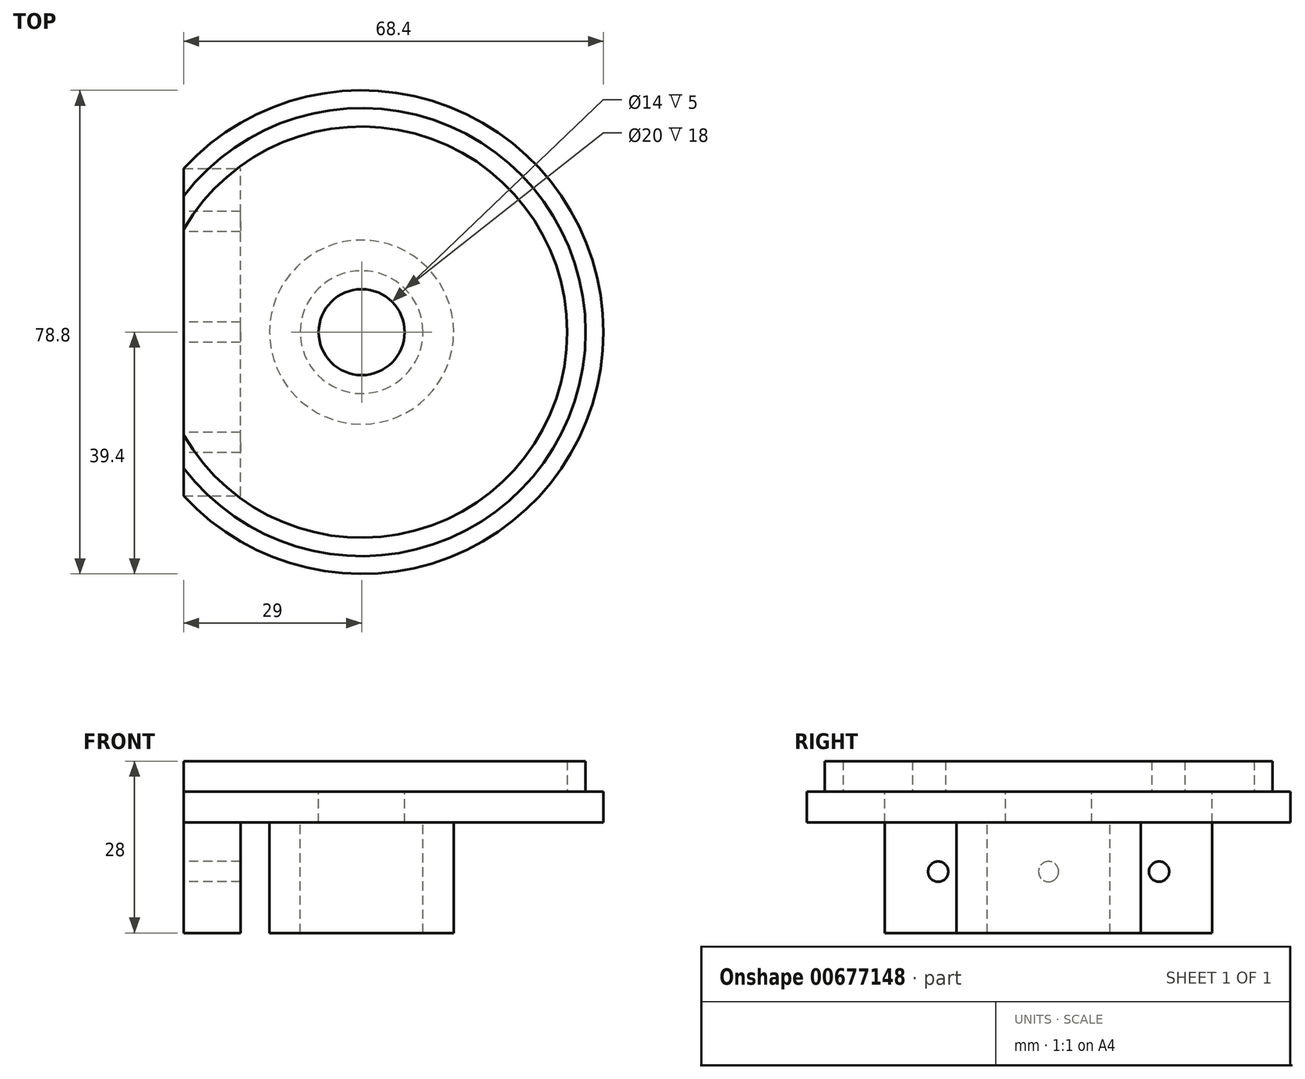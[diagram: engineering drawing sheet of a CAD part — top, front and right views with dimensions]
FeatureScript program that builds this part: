
annotation { "Feature Type Name" : "Feature", "Feature Type Description" : "" }
export const myFeature = defineFeature(function(context is Context, id is Id, definition is map)
    precondition{}
    {
        {
            var Q0;
            Q0=qCreatedBy(makeId("Top.planeOp"),FACE);
            var sketch = newSketch(context, id + "F0", { "sketchPlane" : qUnion([Q0])});
            skArc(sketch, "E0", {"start": v(-29, -26.67) * mm, "mid": v(39.4, 0) * mm, "end": v(-29, 26.67) * mm});
            skArc(sketch, "E1", {"start": v(-29, -22.16) * mm, "mid": v(36.5, 0) * mm, "end": v(-29, 22.16) * mm});
            skArc(sketch, "E2", {"start": v(-29, -16.77) * mm, "mid": v(33.5, 0) * mm, "end": v(-29, 16.77) * mm});
            skLineSegment(sketch, "E3", {"start": v(-29, 26.67) * mm, "end": v(-29, -26.67) * mm});
            skCircle(sketch, "E4", {"center": v(0, 0) * mm, "radius": 7 * mm});
            skSolve(sketch);
        }
        {
            var Q0;
            {var subQ0=sQuery(id+"F0.wireOp",EDGE,"E1");Q0=makeQuery(id+"F0.imprint","IMPRINT",FACE,{"disambiguationData":[TD([[makeQuery(id+"F0.imprint","IMPRINT",EDGE,{"derivedFrom":subQ0}),1.0]])]});}
            extrude(context, id + "F1", {"entities" : qUnion([Q0]), "depth" : 5 * mm, "offsetDistance" : 25 * mm});
        }
        {
            var Q0;
            Q0 = qSketchRegion(id + "F0", true);
            extrude(context, id + "F2", {"entities" : qUnion([Q0]), "operationType" : NewBodyOperationType.ADD, "oppositeDirection" : true, "depth" : 5 * mm, "offsetDistance" : 25 * mm});
        }
        {
            var Q0;
            Q0=makeQuery(id+"F2.opExtrude","CAP_FACE",FACE,{"disambiguationData":[OSD([sQuery(id+"F0.wireOp",EDGE,"E0"),sQuery(id+"F0.wireOp",EDGE,"E3"),sQuery(id+"F0.wireOp",EDGE,"2aKWRgC1-vRAT-dxn1-goK3-0HLVw41naZgE")])],"isStart":false});
            var sketch = newSketch(context, id + "F3", { "sketchPlane" : qUnion([Q0])});
            skCircle(sketch, "E5", {"center": v(0, 0) * mm, "radius": 10 * mm});
            skCircle(sketch, "E6", {"center": v(0, 0) * mm, "radius": 15 * mm});
            skSolve(sketch);
        }
        {
            var Q0;
            Q0=makeQuery(id+"F3.imprint","IMPRINT",FACE,{"disambiguationData":[TD([[makeQuery(id+"F3.imprint","IMPRINT",EDGE,{"derivedFrom":sQuery(id+"F3.wireOp",EDGE,"E5")}),-1.0]])]});
            extrude(context, id + "F4", {"entities" : qUnion([Q0]), "operationType" : NewBodyOperationType.ADD, "depth" : 18 * mm, "offsetDistance" : 25 * mm});
        }
        {
            var Q0;
            {var subQ0=sQuery(id+"F0.wireOp",EDGE,"E0");var subQ1=sQuery(id+"F0.wireOp",EDGE,"E3");Q0=makeQuery(id+"F4.boolean.opBoolean","SPLIT",FACE,{"disambiguationData":[TD([makeQuery(id+"F2.opExtrude","SWEPT_FACE",FACE,{"disambiguationData":[OSD([subQ0])]})])],"derivedFrom":makeQuery(id+"F2.opExtrude","CAP_FACE",FACE,{"disambiguationData":[OSD([subQ0,subQ1,sQuery(id+"F0.wireOp",EDGE,"E4")])],"isStart":false})});}
            var sketch = newSketch(context, id + "F5", { "sketchPlane" : qUnion([Q0])});
            skLineSegment(sketch, "E7.bottom", {"start": v(-29, 26.67) * mm, "end": v(-19.72, 26.67) * mm});
            skLineSegment(sketch, "E7.top", {"start": v(-29, -26.67) * mm, "end": v(-19.72, -26.67) * mm});
            skLineSegment(sketch, "E7.left", {"start": v(-29, 26.67) * mm, "end": v(-29, -26.67) * mm});
            skLineSegment(sketch, "E7.right", {"start": v(-19.72, 26.67) * mm, "end": v(-19.72, -26.67) * mm});
            skSolve(sketch);
        }
        {
            var Q0;
            Q0=makeQuery(id+"F5.imprint","IMPRINT",FACE,{"disambiguationData":[TD([[makeQuery(id+"F5.imprint","IMPRINT",EDGE,{"derivedFrom":sQuery(id+"F5.wireOp",EDGE,"E7.bottom")}),-1.0]])]});
            extrude(context, id + "F6", {"entities" : qUnion([Q0]), "operationType" : NewBodyOperationType.ADD, "depth" : 18 * mm, "offsetDistance" : 25 * mm});
        }
        {
            var Q0;
            {var subQ0=sQuery(id+"F0.wireOp",EDGE,"E3");var subQ1=sQuery(id+"F0.wireOp",EDGE,"E1");Q0=makeQuery(id+"F6.boolean.opBoolean","MERGE",FACE,{"derivedFrom":[makeQuery(id+"F2.boolean.opBoolean","MERGE",FACE,{"derivedFrom":[makeQuery(id+"F1.opExtrude","SWEPT_FACE",FACE,{"disambiguationData":[OSD([subQ0]),TDD([makeQuery(id+"F0.imprint","IMPRINT",EDGE,{"disambiguationData":[TD([[makeQuery(id+"F0.imprint","INTERSECT",VERTEX,{"disambiguationData":[OD(1.0)],"derivedFrom":[subQ1,subQ0]}),-1.0]])],"derivedFrom":subQ0})])]}),makeQuery(id+"F1.opExtrude","SWEPT_FACE",FACE,{"disambiguationData":[OSD([subQ0]),TDD([makeQuery(id+"F0.imprint","IMPRINT",EDGE,{"disambiguationData":[TD([[makeQuery(id+"F0.imprint","INTERSECT",VERTEX,{"disambiguationData":[OD(0.0)],"derivedFrom":[subQ1,subQ0]}),1.0]])],"derivedFrom":subQ0})])]}),makeQuery(id+"F2.opExtrude","SWEPT_FACE",FACE,{"disambiguationData":[OSD([subQ0])]})]}),makeQuery(id+"F6.opExtrude","SWEPT_FACE",FACE,{"disambiguationData":[OSD([sQuery(id+"F5.wireOp",EDGE,"E7.left")])]})]});}
            var sketch = newSketch(context, id + "F7", { "sketchPlane" : qUnion([Q0])});
            skCircle(sketch, "E8", {"center": v(-18, -13) * mm, "radius": 1.65 * mm});
            skCircle(sketch, "E9", {"center": v(0, -13) * mm, "radius": 1.65 * mm});
            skCircle(sketch, "E10", {"center": v(18, -13) * mm, "radius": 1.65 * mm});
            skSolve(sketch);
        }
        {
            var Q0;
            Q0=makeQuery(id+"F7.imprint","IMPRINT",FACE,{"disambiguationData":[TD([[makeQuery(id+"F7.imprint","IMPRINT",EDGE,{"derivedFrom":sQuery(id+"F7.wireOp",EDGE,"E8")}),1.0]])]});
            var Q1;
            Q1=makeQuery(id+"F7.imprint","IMPRINT",FACE,{"disambiguationData":[TD([[makeQuery(id+"F7.imprint","IMPRINT",EDGE,{"derivedFrom":sQuery(id+"F7.wireOp",EDGE,"E9")}),1.0]])]});
            var Q2;
            Q2=makeQuery(id+"F7.imprint","IMPRINT",FACE,{"disambiguationData":[TD([[makeQuery(id+"F7.imprint","IMPRINT",EDGE,{"derivedFrom":sQuery(id+"F7.wireOp",EDGE,"E10")}),1.0]])]});
            extrude(context, id + "F8", {"entities" : qUnion([Q0, Q1, Q2]), "operationType" : NewBodyOperationType.REMOVE, "oppositeDirection" : true, "depth" : 11.3 * mm, "offsetDistance" : 25 * mm});
        }
    });
